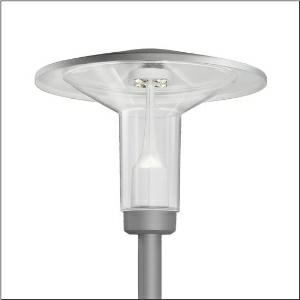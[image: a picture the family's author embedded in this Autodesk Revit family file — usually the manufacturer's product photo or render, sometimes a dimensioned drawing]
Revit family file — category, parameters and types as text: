
# Revit family: laterne_iq___st1_2a_5xa5255kf14h_a0c9
name_source: partatom
category: Lighting Fixtures
units: mm (PartAtom-declared; Revit-internal decimal feet)

## family parameters
Cut with Voids When Loaded = No
Host = Face
Light Source = No
Part Type = Normal
Room Calculation Point = No
Round Connector Dimension = Use Diameter
Shared = No

## types (1)
- --- (1 x LED, 1540 lm, 10 W, 4000K)
    Apparent Load = 10 VA
    CIE Flux Codes = 25 63 94 98 100
    Color Rendering = 70
    Color Temperature = 4000K
    Default Elevation = 1800 mm
    Description = Lantern iQ, mast luminaire, Module 540 iQ-SR, primary light control with 3 zone facetted reflector, of plastic, silver coated, highly specular, structured, primary optical cover: cover, of PMMA, transparent, light distribution: ST1.2a, light emission: direct distribution, primary light characteristic: asymmetric, installation type: post-top, LED, High Power LED, rated luminous flux: 1.540lm, luminous efficacy: 154lm/W, light colour: 740, colour temperature: 4000K, control gear: iQ Street-Remote, control: pre-setting: logarithmic dimming characteristic, Street-Remote, Auto-Match, Temp-Guard, Lumen-Switch, Night-Set, Smart-Wire, Light-Fading, Desk-Remote (wireless, voltage-free reading and setting of iQ features in the workshop via application-optimized NFC function/RFID function), optimised constant luminous flux control (CLO 2.0), with terminal, 6-pole, max. 2.5mm², mains connection: 230..240V, AC, 50/60Hz, start of lifetime: 10W, end of service life: 10W, reduction: 5W, luminaire housing, upper part, of glass-fibre reinforced polyester, coated, Siteco® metallic grey (DB 702S), diameter: 750mm, height: 583mm, spigot size: d x l = 76 x 70mm (post-top) | with reducer (optional accessory) 60 x 70mm, mounting height: 3..5m, post-top mast mounting element, of diecast aluminium, coated, Siteco® metallic grey (DB 702S), Module 540 iQ-SR, traffic white (RAL 9016), equipment: standard, protection rating (complete): IP65, insulation class (complete): insulation class II (safety insulation), certification: CE, ENEC, VDE, packaging unit: 1 piece

Light Distribution: ST1.2a
    Height = 583 mm
    Lamp = 1 x LED
    Lamp Light Flux = 1540 lm
    Lamp Power = 10 W
    Lamp count = 1
    Length = 750 mm
    Luminous efficacy = 154 lm/W
    Manufacturer = Siteco
    ModVariant = No
    Model = 5XA5255KF14H
    Number of Poles = 1
    OnlyDefault = Yes
    Power Factor = 1
    Product Name = Laterne iQ | ST1.2a
    Product group = mast luminaire | pylon top
    ProductGroupID = 6100
    Protection Class = Protection class II
    Protection Degree = IP 65
    RLX_Detail_Level = 1
    RLX_Emergency_Light_Flux = 0 lm
    RLX_Emergency_Type = 0
    RLX_Emergency_Type_DB = No
    RlxData = <blob elided: 93733 chars, md5=113e18ab>
    Socket = socket
    Standby Power = 0 W
    System Light Flux = 1540 lm
    System Power = 10 W
    Type Comments = factory setting: luminous flux: 100 % | dim-lin: 254 | 401 mA
    Type Image = l_1006050.jpg
    URL = http://relux.com
    VarID = @adj_182069
    Voltage = 0 V
    Weight = 0.00 kg
    Width = 0 mm  [stored 0 ft]

note: [stored X ft] marks values corroborated as IEEE doubles in the binary element streams (Revit-internal decimal feet)

## geometry (parser evidence)
native form markers: Blend x4, Sweep x9
no freeform markers — native parametric forms only
